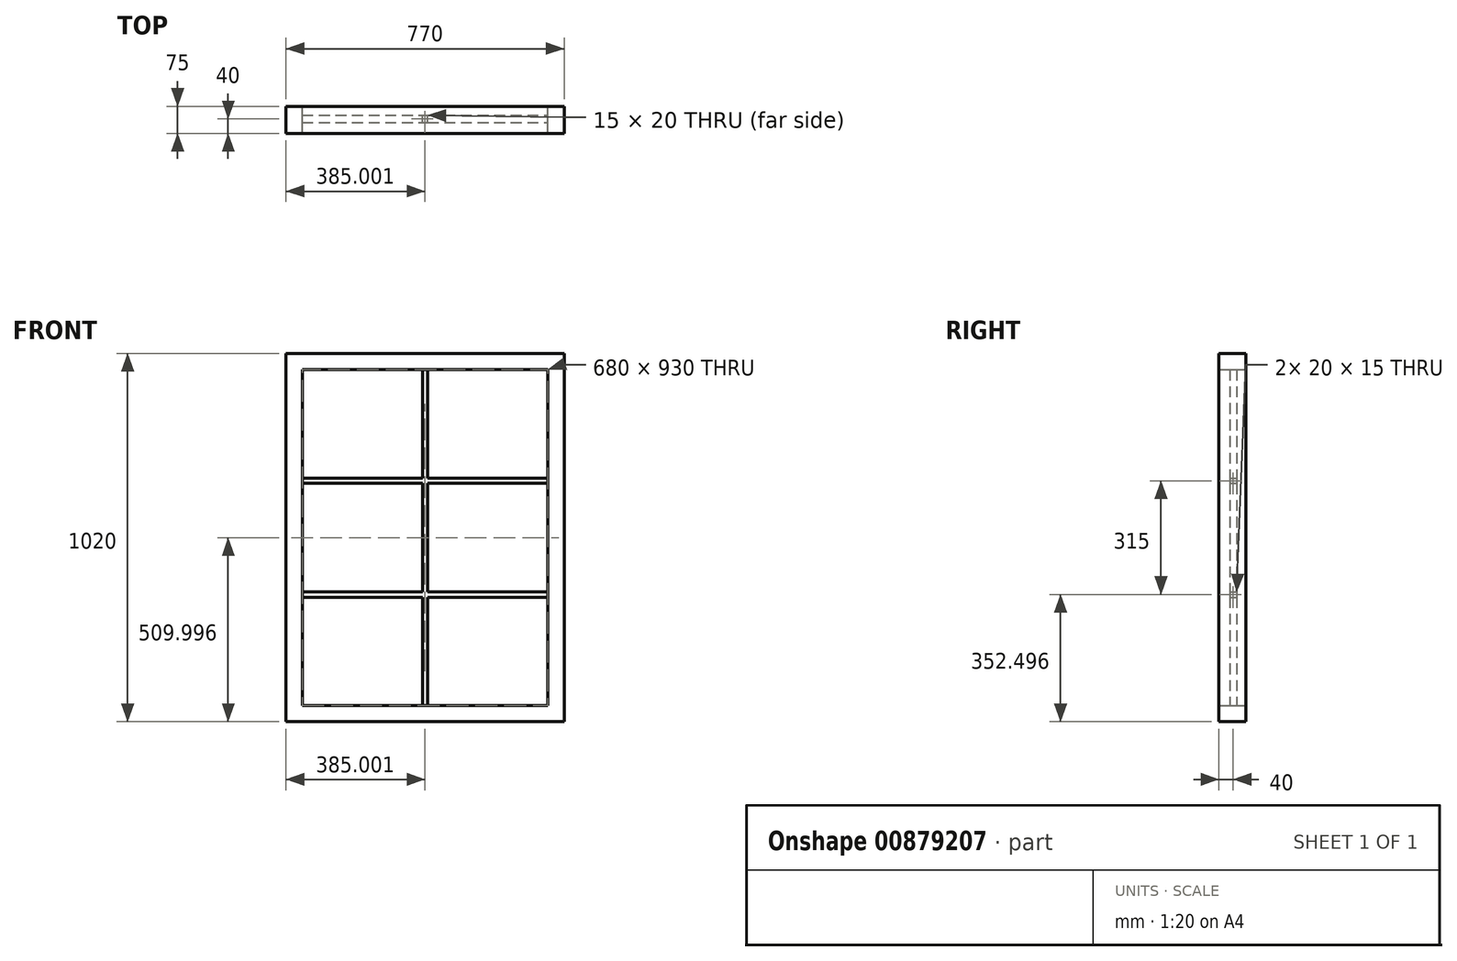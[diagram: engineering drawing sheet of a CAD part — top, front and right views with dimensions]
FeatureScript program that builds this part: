
annotation { "Feature Type Name" : "Feature", "Feature Type Description" : "" }
export const myFeature = defineFeature(function(context is Context, id is Id, definition is map)
    precondition{}
    {
        {
            var Q0;
            Q0=qCreatedBy(makeId("Front.planeOp"),FACE);
            var sketch = newSketch(context, id + "F0", { "sketchPlane" : qUnion([Q0])});
            skLineSegment(sketch, "E0.bottom", {"start": v(-388.14, 502.28) * mm, "end": v(381.86, 502.28) * mm});
            skLineSegment(sketch, "E0.top", {"start": v(-388.14, -517.72) * mm, "end": v(381.86, -517.72) * mm});
            skLineSegment(sketch, "E0.left", {"start": v(-388.14, 502.28) * mm, "end": v(-388.14, -517.72) * mm});
            skLineSegment(sketch, "E0.right", {"start": v(381.86, 502.28) * mm, "end": v(381.86, -517.72) * mm});
            skLineSegment(sketch, "E1.bottom", {"start": v(-343.14, 457.28) * mm, "end": v(336.86, 457.28) * mm});
            skLineSegment(sketch, "E1.top", {"start": v(-343.14, -472.72) * mm, "end": v(336.86, -472.72) * mm});
            skLineSegment(sketch, "E1.left", {"start": v(-343.14, 457.28) * mm, "end": v(-343.14, -472.72) * mm});
            skLineSegment(sketch, "E1.right", {"start": v(336.86, 457.28) * mm, "end": v(336.86, -472.72) * mm});
            skSolve(sketch);
        }
        {
            var Q0;
            Q0=qSketchRegion(id+"F0",true);
            extrude(context, id + "F1", {"entities" : qUnion([Q0]), "depth" : 50 * mm, "offsetDistance" : 25 * mm, "hasSecondDirection" : true, "secondDirectionOppositeDirection" : true, "secondDirectionDepth" : 25 * mm});
        }
        {
            var Q0;
            Q0=qCreatedBy(makeId("Front.planeOp"),FACE);
            var sketch = newSketch(context, id + "F2", { "sketchPlane" : qUnion([Q0])});
            skLineSegment(sketch, "E2.bottom", {"start": v(-10.64, 457.28) * mm, "end": v(4.36, 457.28) * mm});
            skLineSegment(sketch, "E2.top", {"start": v(-10.64, -472.72) * mm, "end": v(4.36, -472.72) * mm});
            skLineSegment(sketch, "E2.left", {"start": v(-10.64, 457.28) * mm, "end": v(-10.64, 157.28) * mm});
            skLineSegment(sketch, "E2.right", {"start": v(4.36, 457.28) * mm, "end": v(4.36, 157.28) * mm});
            skLineSegment(sketch, "E3.bottom", {"start": v(-343.14, 157.28) * mm, "end": v(-10.64, 157.28) * mm});
            skLineSegment(sketch, "E3.top", {"start": v(-343.14, 142.28) * mm, "end": v(-10.64, 142.28) * mm});
            skLineSegment(sketch, "E3.left", {"start": v(-343.14, 157.28) * mm, "end": v(-343.14, 142.28) * mm});
            skLineSegment(sketch, "E3.right", {"start": v(336.86, 157.28) * mm, "end": v(336.86, 142.28) * mm});
            skLineSegment(sketch, "E4.bottom", {"start": v(-343.14, -157.72) * mm, "end": v(-10.64, -157.72) * mm});
            skLineSegment(sketch, "E4.top", {"start": v(-343.14, -172.72) * mm, "end": v(-10.64, -172.72) * mm});
            skLineSegment(sketch, "E4.left", {"start": v(-343.14, -157.72) * mm, "end": v(-343.14, -172.72) * mm});
            skLineSegment(sketch, "E4.right", {"start": v(336.86, -157.72) * mm, "end": v(336.86, -172.72) * mm});
            skLineSegment(sketch, "E5.trimOffspring", {"start": v(4.36, 157.28) * mm, "end": v(336.86, 157.28) * mm});
            skLineSegment(sketch, "E6.trimOffspring", {"start": v(-10.64, 142.28) * mm, "end": v(-10.64, -157.72) * mm});
            skLineSegment(sketch, "E7.trimOffspring", {"start": v(4.36, 142.28) * mm, "end": v(336.86, 142.28) * mm});
            skLineSegment(sketch, "E8.trimOffspring", {"start": v(4.36, 142.28) * mm, "end": v(4.36, -157.72) * mm});
            skLineSegment(sketch, "E9.trimOffspring", {"start": v(4.36, -172.72) * mm, "end": v(336.86, -172.72) * mm});
            skLineSegment(sketch, "E10.trimOffspring", {"start": v(4.36, -157.72) * mm, "end": v(336.86, -157.72) * mm});
            skLineSegment(sketch, "E11.trimOffspring", {"start": v(-10.64, -172.72) * mm, "end": v(-10.64, -472.72) * mm});
            skLineSegment(sketch, "E12.trimOffspring", {"start": v(4.36, -172.72) * mm, "end": v(4.36, -472.72) * mm});
            skSolve(sketch);
        }
        {
            var Q0;
            Q0=qSketchRegion(id+"F2",true);
            extrude(context, id + "F3", {"entities" : qUnion([Q0]), "operationType" : NewBodyOperationType.ADD, "depth" : 20 * mm, "offsetDistance" : 25 * mm});
        }
    });
